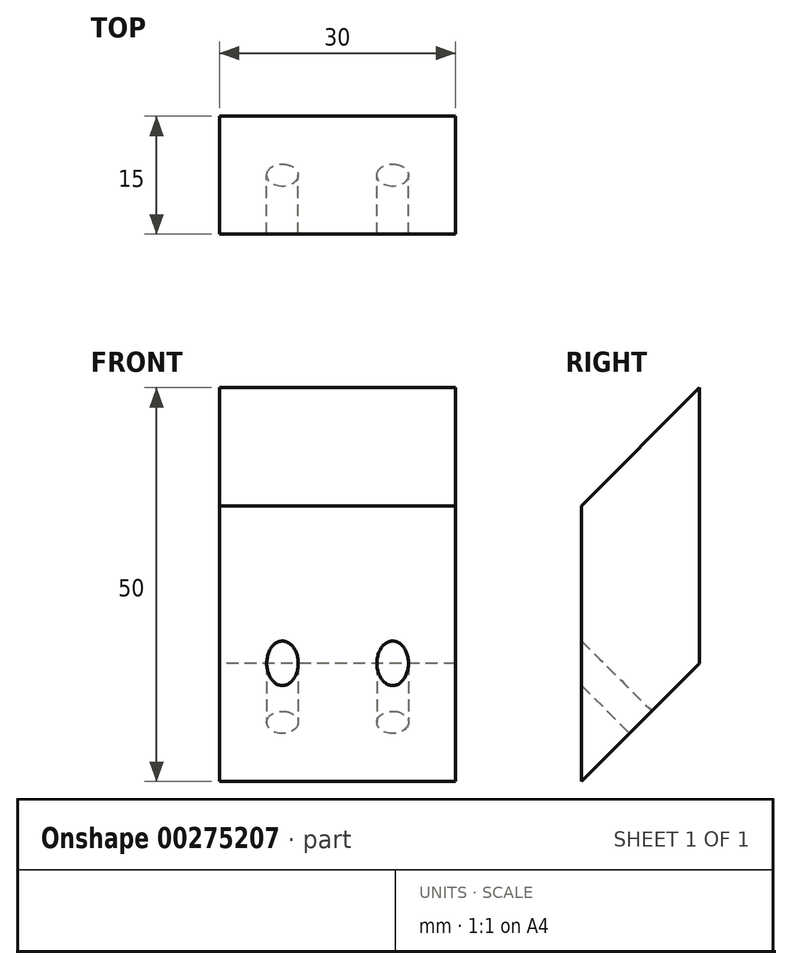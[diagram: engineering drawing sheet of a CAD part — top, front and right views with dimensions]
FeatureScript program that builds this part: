
annotation { "Feature Type Name" : "Feature", "Feature Type Description" : "" }
export const myFeature = defineFeature(function(context is Context, id is Id, definition is map)
    precondition{}
    {
        {
            var Q0;
            Q0=qCreatedBy(makeId("Top.planeOp"),FACE);
            var sketch = newSketch(context, id + "F0", { "sketchPlane" : qUnion([Q0])});
            skLineSegment(sketch, "E0.bottom", {"start": v(-38.12, 18.88) * mm, "end": v(-8.12, 18.88) * mm});
            skLineSegment(sketch, "E0.top", {"start": v(-38.12, 3.88) * mm, "end": v(-8.12, 3.88) * mm});
            skLineSegment(sketch, "E0.left", {"start": v(-38.12, 18.88) * mm, "end": v(-38.12, 3.88) * mm});
            skLineSegment(sketch, "E0.right", {"start": v(-8.12, 18.88) * mm, "end": v(-8.12, 3.88) * mm});
            skSolve(sketch);
        }
        {
            var Q0;
            Q0=makeQuery(id+"F0.imprint","IMPRINT",FACE,{"disambiguationData":[TD([[makeQuery(id+"F0.imprint","IMPRINT",EDGE,{"derivedFrom":sQuery(id+"F0.wireOp",EDGE,"E0.bottom")}),-1.0]])]});
            extrude(context, id + "F1", {"entities" : qUnion([Q0]), "depth" : 50 * mm});
        }
        {
            var Q0;
            Q0=makeQuery(id+"F1.opExtrude","SWEPT_FACE",FACE,{"disambiguationData":[OSD([sQuery(id+"F0.wireOp",EDGE,"E0.left")])]});
            var sketch = newSketch(context, id + "F2", { "sketchPlane" : qUnion([Q0])});
            skLineSegment(sketch, "E1", {"start": v(-18.88, 50) * mm, "end": v(-3.88, 35) * mm});
            skLineSegment(sketch, "E2", {"start": v(-3.88, 0) * mm, "end": v(-18.88, 15) * mm});
            skSolve(sketch);
        }
        {
            var Q0;
            {var subQ0=sQuery(id+"F2.wireOp",EDGE,"E1");Q0=makeQuery(id+"F2.imprint","IMPRINT",FACE,{"disambiguationData":[TD([[makeQuery(id+"F2.imprint","IMPRINT",EDGE,{"derivedFrom":subQ0}),1.0]])]});}
            var Q1;
            {var subQ0=sQuery(id+"F2.wireOp",EDGE,"E2");Q1=makeQuery(id+"F2.imprint","IMPRINT",FACE,{"disambiguationData":[TD([[makeQuery(id+"F2.imprint","IMPRINT",EDGE,{"derivedFrom":subQ0}),1.0]])]});}
            extrude(context, id + "F3", {"entities" : qUnion([Q0, Q1]), "operationType" : NewBodyOperationType.REMOVE, "endBound" : BoundingType.THROUGH_ALL, "oppositeDirection" : true, "depth" : 25 * mm});
        }
        {
            var Q0;
            Q0=makeQuery(id+"F3.boolean.opBoolean","COPY",FACE,{"derivedFrom":makeQuery(id+"F3.opExtrude","SWEPT_FACE",FACE,{"disambiguationData":[OSD([sQuery(id+"F2.wireOp",EDGE,"E2")])]})});
            var sketch = newSketch(context, id + "F4", { "sketchPlane" : qUnion([Q0])});
            skLineSegment(sketch, "E3", {"start": v(38.12, 13.35) * mm, "end": v(8.12, 13.35) * mm, "construction": true});
            skLineSegment(sketch, "E4", {"start": v(23.12, 23.96) * mm, "end": v(23.12, 2.74) * mm, "construction": true});
            skPoint(sketch, "E5", {"position": v(30.12, 13.35) * mm});
            skPoint(sketch, "E6", {"position": v(16.12, 13.35) * mm});
            skSolve(sketch);
        }
        {
            var Q0;
            Q0=sQuery(id+"F4.wireOp",VERTEX,"E5");
            var Q1;
            Q1=sQuery(id+"F4.wireOp",VERTEX,"E6");
            var Q2;
            Q2=makeQuery(id+"F1.opExtrude","SWEPT_BODY",BODY,{"disambiguationData":[OSD([sQuery(id+"F0.wireOp",EDGE,"E0.bottom"),sQuery(id+"F0.wireOp",EDGE,"E0.top"),sQuery(id+"F0.wireOp",EDGE,"E0.left"),sQuery(id+"F0.wireOp",EDGE,"E0.right")])]});
            hole(context, id + "F5", {"style" : HoleStyle.SIMPLE, "endStyle" : HoleEndStyle.THROUGH, "holeDiameter" : 4 * mm, "isTappedThrough" : true, "tappedDepth" : 12 * mm, "tapClearance" : 3, "startFromSketch" : true, "locations" : qUnion([Q0, Q1]), "scope" : qUnion([Q2])});
        }
    });
